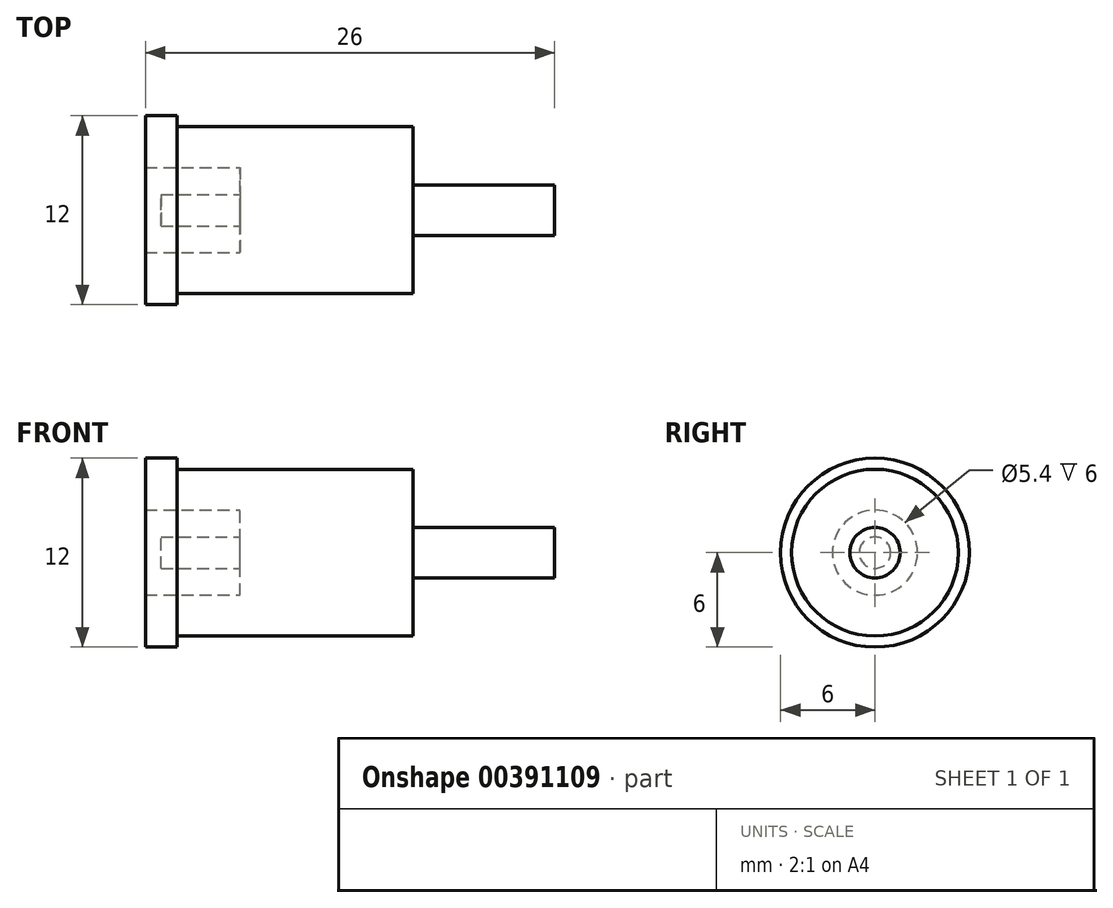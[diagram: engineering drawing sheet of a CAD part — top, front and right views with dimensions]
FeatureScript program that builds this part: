
annotation { "Feature Type Name" : "Feature", "Feature Type Description" : "" }
export const myFeature = defineFeature(function(context is Context, id is Id, definition is map)
    precondition{}
    {
        {
            var Q0;
            Q0=qCreatedBy(makeId("Front.planeOp"),FACE);
            var sketch = newSketch(context, id + "F0", { "sketchPlane" : qUnion([Q0])});
            skLineSegment(sketch, "E0", {"start": v(0, 2.7) * mm, "end": v(0, 6) * mm});
            skLineSegment(sketch, "E1", {"start": v(0, 6) * mm, "end": v(2, 6) * mm});
            skLineSegment(sketch, "E2", {"start": v(2, 6) * mm, "end": v(2, 5.3) * mm});
            skLineSegment(sketch, "E3", {"start": v(2, 5.3) * mm, "end": v(17, 5.3) * mm});
            skLineSegment(sketch, "E4", {"start": v(17, 5.3) * mm, "end": v(17, 1.6) * mm});
            skLineSegment(sketch, "E5", {"start": v(17, 1.6) * mm, "end": v(26, 1.6) * mm});
            skLineSegment(sketch, "E6", {"start": v(26, 1.6) * mm, "end": v(26, 0) * mm});
            skLineSegment(sketch, "E7", {"start": v(26, 0) * mm, "end": v(1, 0) * mm});
            skLineSegment(sketch, "E8", {"start": v(0, 2.7) * mm, "end": v(6, 2.7) * mm});
            skLineSegment(sketch, "E9", {"start": v(6, 2.7) * mm, "end": v(6, 1) * mm});
            skLineSegment(sketch, "E10", {"start": v(6, 1) * mm, "end": v(1, 1) * mm});
            skLineSegment(sketch, "E11", {"start": v(1, 1) * mm, "end": v(1, 0) * mm});
            skPoint(sketch, "E12.orphan", {"position": v(0, 0) * mm});
            skSolve(sketch);
        }
        {
            var Q0;
            Q0=qSketchRegion(id+"F0",true);
            var Q1;
            Q1=sQuery(id+"F0.wireOp",EDGE,"E7");
            revolve(context, id + "F1", {"entities" : qUnion([Q0]), "axis" : qUnion([Q1]), "revolveType" : RevolveType.FULL});
        }
    });
